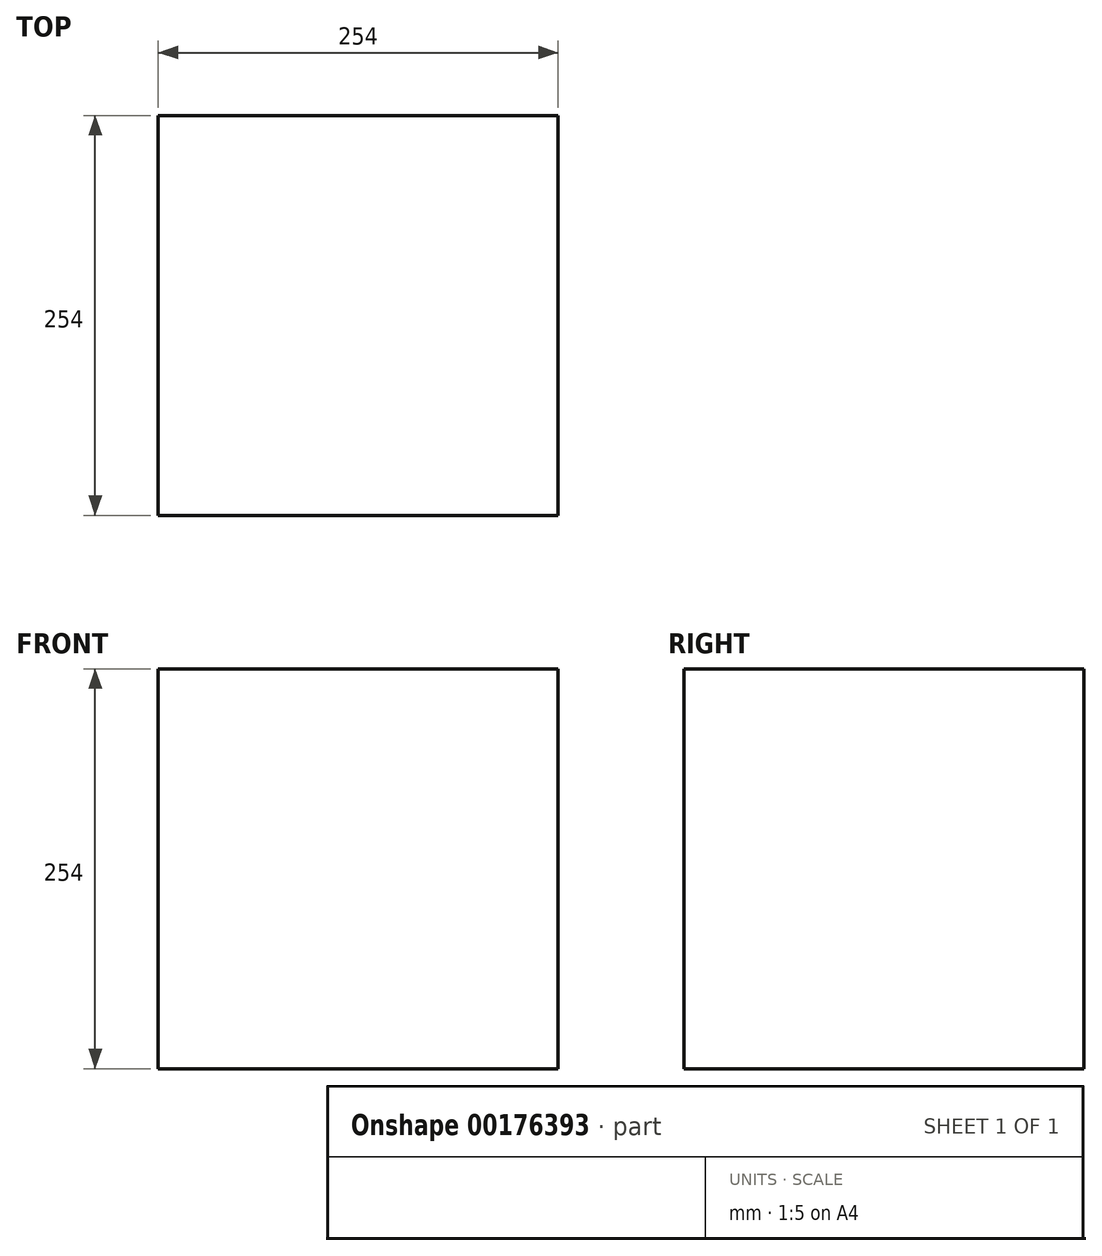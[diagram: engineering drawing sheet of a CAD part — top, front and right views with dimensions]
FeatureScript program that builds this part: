
annotation { "Feature Type Name" : "Feature", "Feature Type Description" : "" }
export const myFeature = defineFeature(function(context is Context, id is Id, definition is map)
    precondition{}
    {
        {
            var Q0;
            Q0=qCreatedBy(makeId("Top.planeOp"),FACE);
            var sketch = newSketch(context, id + "F0", { "sketchPlane" : qUnion([Q0])});
            skCircle(sketch, "E0.cCircle", {"center": v(0, 0) * mm, "radius": 127 * mm, "construction": true});
            skLineSegment(sketch, "E0.0", {"start": v(-127, -127) * mm, "end": v(-127, 127) * mm});
            skLineSegment(sketch, "E0.1", {"start": v(-127, 127) * mm, "end": v(127, 127) * mm});
            skLineSegment(sketch, "E0.2", {"start": v(127, 127) * mm, "end": v(127, -127) * mm});
            skLineSegment(sketch, "E0.3", {"start": v(127, -127) * mm, "end": v(-127, -127) * mm});
            skPoint(sketch, "E0.0.midPoint", {"position": v(-127, 0) * mm});
            skSolve(sketch);
        }
        {
            var Q0;
            Q0=makeQuery(id+"F0.imprint","IMPRINT",FACE,{"disambiguationData":[TD([[makeQuery(id+"F0.imprint","IMPRINT",EDGE,{"derivedFrom":sQuery(id+"F0.wireOp",EDGE,"E0.0")}),-1.0]])]});
            extrude(context, id + "F1", {"entities" : qUnion([Q0]), "depth" : 254 * mm});
        }
        {
            var Q0;
            Q0=makeQuery(id+"F1.opExtrude","SWEPT_FACE",FACE,{"disambiguationData":[OSD([sQuery(id+"F0.wireOp",EDGE,"E0.3")])]});
            var sketch = newSketch(context, id + "F2", { "sketchPlane" : qUnion([Q0])});
            skLineSegment(sketch, "E1", {"start": v(127, 254) * mm, "end": v(-127, 0) * mm});
            skSolve(sketch);
        }
        {
            var Q0;
            Q0=makeQuery(id+"F1.opExtrude","CAP_FACE",FACE,{"disambiguationData":[OSD([sQuery(id+"F0.wireOp",EDGE,"E0.0"),sQuery(id+"F0.wireOp",EDGE,"E0.1"),sQuery(id+"F0.wireOp",EDGE,"E0.2"),sQuery(id+"F0.wireOp",EDGE,"E0.3")])],"isStart":false});
            var sketch = newSketch(context, id + "F3", { "sketchPlane" : qUnion([Q0])});
            skLineSegment(sketch, "E2", {"start": v(127, -127) * mm, "end": v(-127, 127) * mm});
            skSolve(sketch);
        }
        {
            var Q0;
            Q0=makeQuery(id+"F1.opExtrude","SWEPT_FACE",FACE,{"disambiguationData":[OSD([sQuery(id+"F0.wireOp",EDGE,"E0.0")])]});
            var sketch = newSketch(context, id + "F4", { "sketchPlane" : qUnion([Q0])});
            skLineSegment(sketch, "E3", {"start": v(-127, 254) * mm, "end": v(127, 0) * mm});
            skSolve(sketch);
        }
        {
            var Q0;
            Q0=makeQuery(id+"F1.opExtrude","SWEPT_FACE",FACE,{"disambiguationData":[OSD([sQuery(id+"F0.wireOp",EDGE,"E0.2")])]});
            var sketch = newSketch(context, id + "F5", { "sketchPlane" : qUnion([Q0])});
            skLineSegment(sketch, "E4", {"start": v(-127, 254) * mm, "end": v(127, 0) * mm});
            skSolve(sketch);
        }
        {
            var Q0;
            Q0=makeQuery(id+"F1.opExtrude","SWEPT_FACE",FACE,{"disambiguationData":[OSD([sQuery(id+"F0.wireOp",EDGE,"E0.1")])]});
            var sketch = newSketch(context, id + "F6", { "sketchPlane" : qUnion([Q0])});
            skLineSegment(sketch, "E5", {"start": v(127, 254) * mm, "end": v(-127, 0) * mm});
            skSolve(sketch);
        }
        {
            var Q0;
            Q0=makeQuery(id+"F1.opExtrude","CAP_FACE",FACE,{"disambiguationData":[OSD([sQuery(id+"F0.wireOp",EDGE,"E0.0"),sQuery(id+"F0.wireOp",EDGE,"E0.1"),sQuery(id+"F0.wireOp",EDGE,"E0.2"),sQuery(id+"F0.wireOp",EDGE,"E0.3")])],"isStart":true});
            var sketch = newSketch(context, id + "F7", { "sketchPlane" : qUnion([Q0])});
            skLineSegment(sketch, "E6", {"start": v(127, -127) * mm, "end": v(-127, 127) * mm});
            skSolve(sketch);
        }
    });
